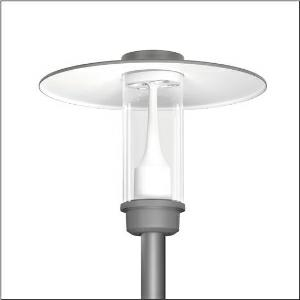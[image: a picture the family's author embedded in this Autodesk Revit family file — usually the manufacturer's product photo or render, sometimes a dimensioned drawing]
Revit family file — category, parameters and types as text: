
# Revit family: litepole_2_iq___pl1_2s_5xa5425jf14h_0ba0
name_source: partatom
category: Lighting Fixtures
units: mm (PartAtom-declared; Revit-internal decimal feet)

## family parameters
Cut with Voids When Loaded = No
Host = Face
Light Source = No
Part Type = Normal
Room Calculation Point = No
Round Connector Dimension = Use Diameter
Shared = No

## types (1)
- --- (1 x LED, 2990 lm, 19.3 W, 3000K)
    Apparent Load = 19 VA
    CIE Flux Codes = 22 60 92 98 100
    Color Rendering = 70
    Color Temperature = 3000K
    Default Elevation = 1800 mm
    Description = Litepole 2 iQ, mast luminaire, Module 540 iQ-SR, primary light control with 3 zone facetted reflector, of plastic, silver coated, highly specular, structured, primary optical cover: cover, of PMMA, transparent, light distribution: PL1.2s, light emission: direct distribution, primary light characteristic: symmetric, installation type: post-top, LED, High Power LED, rated luminous flux: 2.990lm, luminous efficacy: 155lm/W, light colour: 730, colour temperature: 3000K, control gear: iQ Street-Remote, control: Auto-Match, Temp-Guard, Lumen-Switch, Night-Set, Smart-Wire, Light-Fading, Desk-Remote (wireless, voltage-free reading and setting of iQ features in the workshop via application-optimized NFC function/RFID function), optimised constant luminous flux control (CLO 2.0), Street-Remote, pre-setting: logarithmic dimming characteristic, with terminal, 6-pole, max. 2.5mm², mains connection: 230..240V, AC, 50/60Hz, start of lifetime: 19W, end of service life: 21W, reduction: 10W, luminaire housing, upper part, of aluminium, coated, Siteco® metallic grey (DB 702S), diameter: 750mm, height: 590mm, spigot size: d x l = 76 x 70mm (post-top) | with reducer (optional accessory) 60 x 70mm, mounting height: 3..5m, post-top mast mounting element, of diecast aluminium, coated, Siteco® metallic grey (DB 702S), Module 540 iQ-SR, traffic white (RAL 9016), equipment: standard, protection rating (complete): IP65, insulation class (complete): insulation class II (safety insulation), certification: CE, ENEC, VDE, packaging unit: 1 piece

Light Distribution: PL1.2s
    Height = 590 mm
    Lamp = 1 x LED
    Lamp Light Flux = 2990 lm
    Lamp Power = 19.3 W
    Lamp count = 1
    Length = 750 mm
    Luminous efficacy = 155 lm/W
    Manufacturer = Siteco
    ModVariant = No
    Model = 5XA5425JF14H
    Number of Poles = 1
    OnlyDefault = Yes
    Power Factor = 1
    Product Name = Litepole 2 iQ | PL1.2s
    Product group = mast luminaire | pylon top
    ProductGroupID = 6100
    Protection Class = Protection class II
    Protection Degree = IP 65
    RLX_Detail_Level = 1
    RLX_Emergency_Light_Flux = 0 lm
    RLX_Emergency_Type = 0
    RLX_Emergency_Type_DB = No
    RlxData = <blob elided: 29393 chars, md5=66113369>
    Socket = socket
    Standby Power = 0 W
    System Light Flux = 2990 lm
    System Power = 19 W
    Type Comments = factory setting: luminous flux: 100 % | dim-lin: 254 | 403 mA
    Type Image = l_1006518.jpg
    URL = http://relux.com
    VarID = @adj_144646
    Voltage = 0 V
    Weight = 0.00 kg
    Width = 0 mm  [stored 0 ft]

note: [stored X ft] marks values corroborated as IEEE doubles in the binary element streams (Revit-internal decimal feet)

## geometry (parser evidence)
native form markers: Blend x4, Sweep x8
no freeform markers — native parametric forms only
